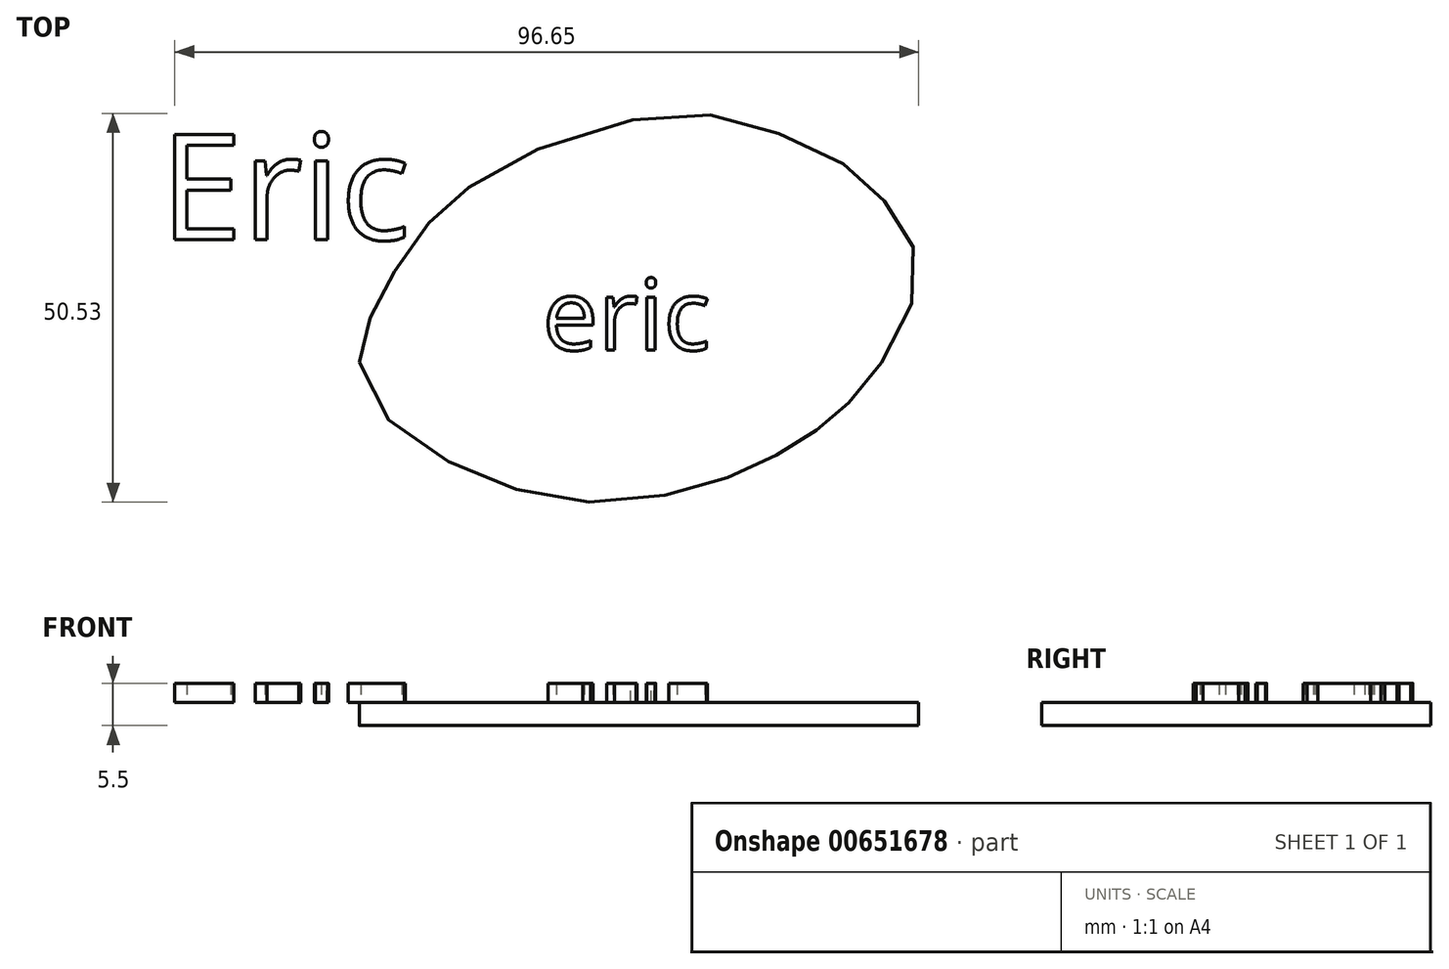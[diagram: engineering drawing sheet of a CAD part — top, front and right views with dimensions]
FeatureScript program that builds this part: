
annotation { "Feature Type Name" : "Feature", "Feature Type Description" : "" }
export const myFeature = defineFeature(function(context is Context, id is Id, definition is map)
    precondition{}
    {
        {
            var Q0;
            Q0=qCreatedBy(makeId("Top.planeOp"),FACE);
            var sketch = newSketch(context, id + "F0", { "sketchPlane" : qUnion([Q0])});
            skLineSegment(sketch, "E0", {"start": v(20.46, 30.17) * mm, "end": v(99.63, 41.65) * mm, "construction": true});
            skFitSpline(sketch, "E1", {"points": [v(22.2, 30.42) * mm, v(23.13, 35.2) * mm, v(25.23, 39.59) * mm, v(29.72, 46.77) * mm, v(33.71, 50.96) * mm, v(41.95, 56.57) * mm, v(61.45, 62.58) * mm, v(72.3, 61.58) * mm, v(83.67, 57.05) * mm, v(89.36, 52.52) * mm, v(93.27, 47.24) * mm, v(94.78, 40.94) * mm, v(90.79, 31.9) * mm, v(87.23, 26.37) * mm, v(82.96, 23.1) * mm, v(81, 21.1) * mm, v(76.2, 18.33) * mm, v(70.34, 15.56) * mm, v(61.27, 13.05) * mm, v(48.3, 12.54) * mm, v(37.09, 16.06) * mm, v(26.78, 22.1) * mm, v(22.2, 30.42) * mm]});
            skSolve(sketch);
        }
        {
            var Q0;
            Q0=makeQuery(id+"F0.imprint","IMPRINT",FACE,{"disambiguationData":[TD([[makeQuery(id+"F0.imprint","IMPRINT",EDGE,{"derivedFrom":sQuery(id+"F0.wireOp",EDGE,"E1")}),-1.0]])]});
            extrude(context, id + "F1", {"entities" : qUnion([Q0]), "depth" : 3 * mm, "offsetDistance" : 25 * mm});
        }
        {
            var Q0;
            Q0=makeQuery(id+"F1.opExtrude","CAP_FACE",FACE,{"disambiguationData":[OSD([sQuery(id+"F0.wireOp",EDGE,"E1")])],"isStart":false});
            var sketch = newSketch(context, id + "F2", { "sketchPlane" : qUnion([Q0])});
            skText(sketch, "E2", { "text": "Eric", "fontName": "OpenSans-Regular.ttf"});
            skText(sketch, "E3", { "text": "eric", "fontName": "OpenSans-Regular.ttf"});
            const initialGuessF2  = {"E2": [-0.00368, 0.04636, 1, 0, 0.01381], "E3": [0.04598, 0.03203, 1, 0, 0.00925]};
            skSetInitialGuess(sketch, initialGuessF2);
            skSolve(sketch);
        }
        {
            var Q0;
            Q0 = qSketchRegion(id + "F2", true);
            extrude(context, id + "F3", {"entities" : qUnion([Q0]), "operationType" : NewBodyOperationType.ADD, "depth" : 2.5 * mm, "offsetDistance" : 25 * mm});
        }
    });
